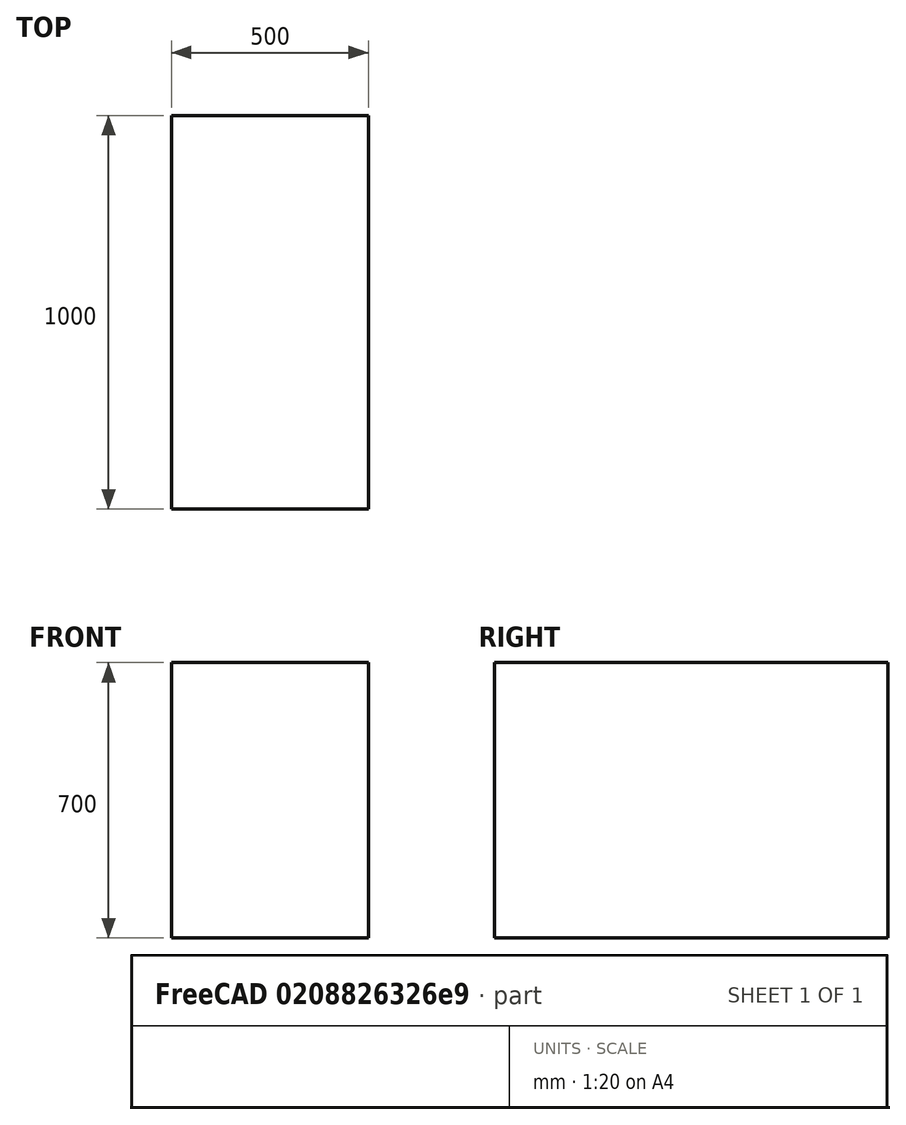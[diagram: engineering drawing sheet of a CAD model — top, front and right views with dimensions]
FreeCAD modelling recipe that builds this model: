
FCSTD DOCUMENT  (FreeCAD 1.0R39109 (Git))
Label: beam
License: All rights reserved
LicenseURL: http://en.wikipedia.org/wiki/All_rights_reserved
objects: Sketcher::SketchObject×1, PartDesign::Pad×1, PartDesign::Body×1
note: 6 computed .brp shape members not serialized (recipe doc carries the construction recipe); baked Part::Feature solids carry a one-line shape summary decoded from their .brp

FEATURE [Sketcher::SketchObject] Sketch
  ArcFitTolerance = 1e-06
  FullyConstrained = true
  MakeInternals = false
  Placement = pos=(0,0,0) rot=(1,0,0;1.5708rad)
  sketch-geometry (5):
    g0: LineSegment StartX=250 StartY=-350 StartZ=0 EndX=250 EndY=350 EndZ=0
    g1: LineSegment StartX=250 StartY=350 StartZ=0 EndX=-250 EndY=350 EndZ=0
    g2: LineSegment StartX=-250 StartY=350 StartZ=0 EndX=-250 EndY=-350 EndZ=0
    g3: LineSegment StartX=-250 StartY=-350 StartZ=0 EndX=250 EndY=-350 EndZ=0
    g4: GeomPoint [constr] X=0 Y=0 Z=0
  constraints (12):
    c: Coincident(g0,g1)
    c: Coincident(g1,g2)
    c: Coincident(g2,g3)
    c: Coincident(g3,g0)
    c: Vertical(g0)
    c: Vertical(g2)
    c: Horizontal(g1)
    c: Horizontal(g3)
    c: Symmetric(g2,g0,g4)
    c: Coincident(g4,g-1)
    c: DistanceX(g1,g1) = 500  'width'
    c: DistanceY(g2,g2) = 700  'depth'
FEATURE [PartDesign::Pad] Pad  label="length"
  Direction = (0,-1,-2e-16)
  Length = 1000
  Length2 = 10
  Placement = pos=(0,0,0) rot=(1,0,0;1.5708rad)
  Profile = -> Sketch
  ReferenceAxis = -> Sketch [N_Axis]
  Reversed = true
  Suppressed = false
  Type = 0
FEATURE [PartDesign::Body] Body  label="beam"
  AllowCompound = false
  Group = -> [Sketch,Pad]
  Origin = -> Origin
  Tip = -> Pad
  cross_section = Rectangular
